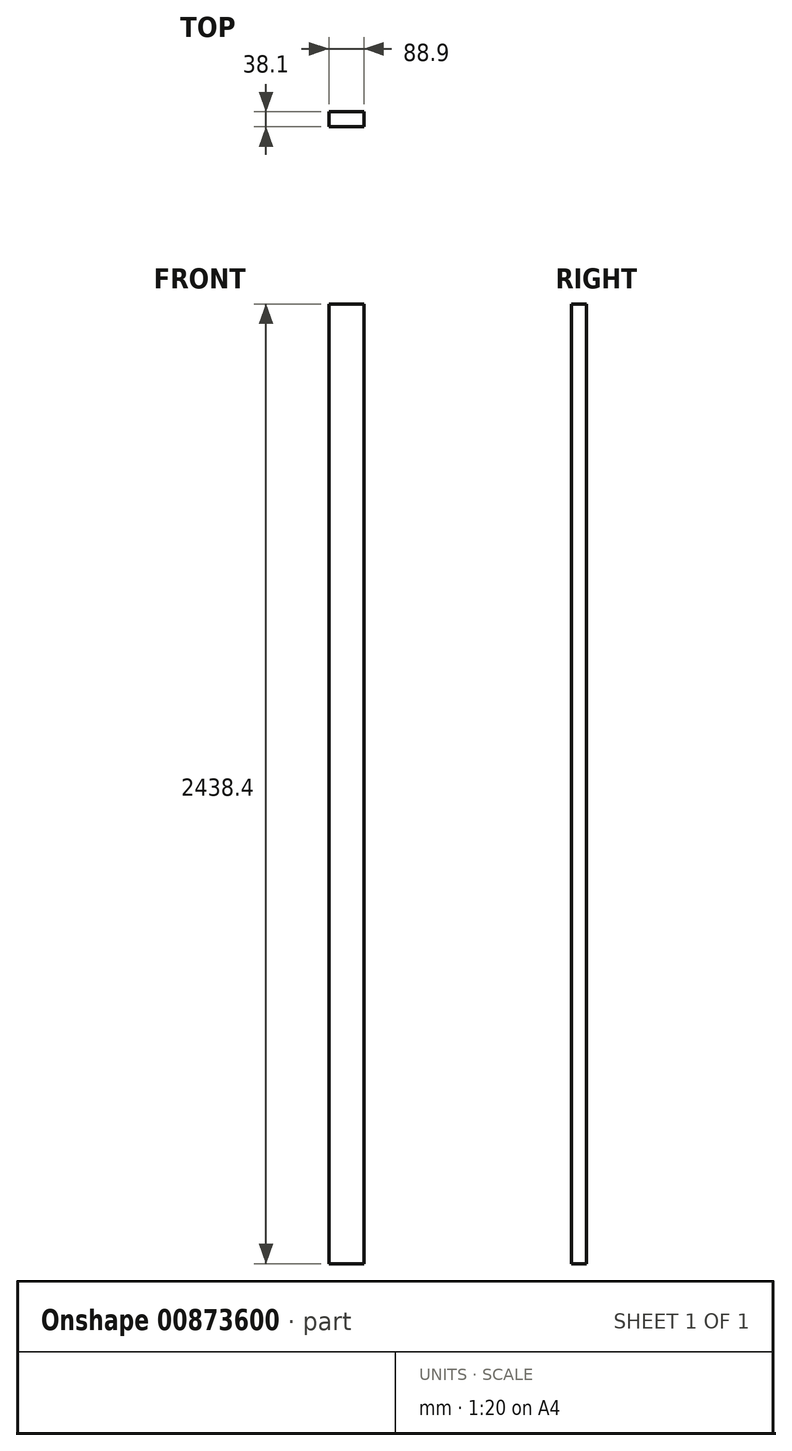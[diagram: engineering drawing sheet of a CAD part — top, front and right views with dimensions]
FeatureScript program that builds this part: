
annotation { "Feature Type Name" : "Feature", "Feature Type Description" : "" }
export const myFeature = defineFeature(function(context is Context, id is Id, definition is map)
    precondition{}
    {
        {
            var Q0;
            Q0=qCreatedBy(makeId("Top.planeOp"),FACE);
            var sketch = newSketch(context, id + "F0", { "sketchPlane" : qUnion([Q0])});
            skLineSegment(sketch, "E0.bottom", {"start": v(0, 0) * mm, "end": v(88.9, 0) * mm});
            skLineSegment(sketch, "E0.top", {"start": v(0, 38.1) * mm, "end": v(88.9, 38.1) * mm});
            skLineSegment(sketch, "E0.left", {"start": v(0, 0) * mm, "end": v(0, 38.1) * mm});
            skLineSegment(sketch, "E0.right", {"start": v(88.9, 0) * mm, "end": v(88.9, 38.1) * mm});
            skSolve(sketch);
        }
        {
            var Q0;
            Q0 = qSketchRegion(id + "F0", true);
            extrude(context, id + "F1", {"entities" : qUnion([Q0]), "depth" : 2438.4 * mm, "offsetDistance" : 25.4 * mm});
        }
    });
